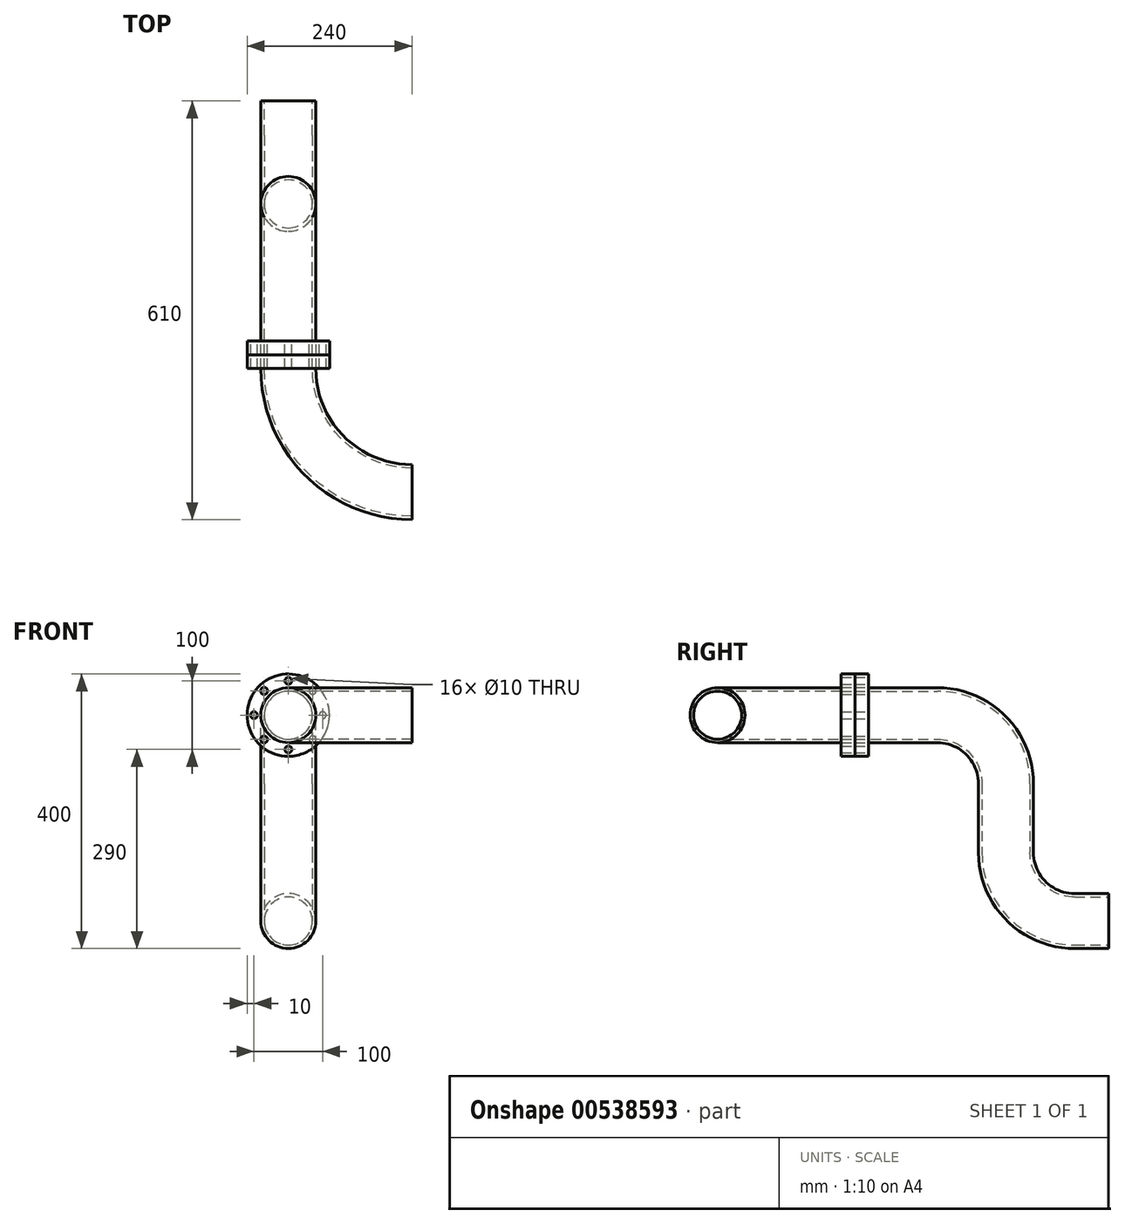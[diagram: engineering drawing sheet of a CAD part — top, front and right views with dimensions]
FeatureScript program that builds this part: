
annotation { "Feature Type Name" : "Feature", "Feature Type Description" : "" }
export const myFeature = defineFeature(function(context is Context, id is Id, definition is map)
    precondition{}
    {
        {
            var Q0;
            Q0=qCreatedBy(makeId("Front.planeOp"),FACE);
            var sketch = newSketch(context, id + "F0", { "sketchPlane" : qUnion([Q0])});
            skCircle(sketch, "E0", {"center": v(0, 0) * mm, "radius": 60 * mm});
            skCircle(sketch, "E1", {"center": v(0, 50) * mm, "radius": 5 * mm});
            skCircle(sketch, "E2", {"center": v(0, -50) * mm, "radius": 5 * mm});
            skCircle(sketch, "E3", {"center": v(-50, 0) * mm, "radius": 5 * mm});
            skCircle(sketch, "E4.1.0", {"center": v(-35.36, 35.36) * mm, "radius": 5 * mm});
            skCircle(sketch, "E5.1.3.0", {"center": v(-35.36, -35.36) * mm, "radius": 5 * mm});
            skCircle(sketch, "E5.1.5.0", {"center": v(35.36, -35.36) * mm, "radius": 5 * mm});
            skCircle(sketch, "E5.1.7.0", {"center": v(35.36, 35.36) * mm, "radius": 5 * mm});
            skCircle(sketch, "E6", {"center": v(50, 0) * mm, "radius": 5 * mm});
            skCircle(sketch, "E7", {"center": v(0, 0) * mm, "radius": 35 * mm});
            skSolve(sketch);
        }
        {
            var Q0;
            Q0=makeQuery(id+"F0.imprint","IMPRINT",FACE,{"disambiguationData":[TD([[makeQuery(id+"F0.imprint","IMPRINT",EDGE,{"derivedFrom":sQuery(id+"F0.wireOp",EDGE,"E0")}),1.0]])]});
            extrude(context, id + "F1", {"entities" : qUnion([Q0]), "depth" : 20 * mm, "offsetDistance" : 25 * mm});
        }
        {
            var Q0;
            Q0=qCreatedBy(makeId("Front.planeOp"),FACE);
            var sketch = newSketch(context, id + "F2", { "sketchPlane" : qUnion([Q0])});
            skCircle(sketch, "E8", {"center": v(0, 0) * mm, "radius": 35 * mm});
            skCircle(sketch, "E9", {"center": v(0, 0) * mm, "radius": 40 * mm});
            skSolve(sketch);
        }
        {
            var Q0;
            Q0=qCreatedBy(makeId("Right.planeOp"),FACE);
            var sketch = newSketch(context, id + "F3", { "sketchPlane" : qUnion([Q0])});
            skLineSegment(sketch, "E10", {"start": v(0, 0) * mm, "end": v(100, 0) * mm});
            skLineSegment(sketch, "E11", {"start": v(200, -100) * mm, "end": v(200, -200) * mm});
            skLineSegment(sketch, "E12", {"start": v(300, -300) * mm, "end": v(350, -300) * mm});
            skPoint(sketch, "E13.visualSharp", {"position": v(200, 0) * mm});
            skArc(sketch, "E13.filletArc", {"start": v(200, -100) * mm, "mid": v(170.71, -29.29) * mm, "end": v(100, 0) * mm});
            skPoint(sketch, "E14.visualSharp", {"position": v(200, -300) * mm});
            skArc(sketch, "E14.filletArc", {"start": v(200, -200) * mm, "mid": v(229.29, -270.71) * mm, "end": v(300, -300) * mm});
            skSolve(sketch);
        }
        {
            var Q0;
            Q0=makeQuery(id+"F2.imprint","IMPRINT",FACE,{"disambiguationData":[TD([[makeQuery(id+"F2.imprint","IMPRINT",EDGE,{"derivedFrom":sQuery(id+"F2.wireOp",EDGE,"E8")}),-1.0]])]});
            var Q1;
            Q1=sQuery(id+"F3.wireOp",EDGE,"E10");
            var Q2;
            Q2=sQuery(id+"F3.wireOp",EDGE,"E13.filletArc");
            var Q3;
            Q3=sQuery(id+"F3.wireOp",EDGE,"E11");
            var Q4;
            Q4=sQuery(id+"F3.wireOp",EDGE,"E14.filletArc");
            var Q5;
            Q5=sQuery(id+"F3.wireOp",EDGE,"E12");
            sweep(context, id + "F4", {"operationType" : NewBodyOperationType.ADD, "profiles" : qUnion([Q0]), "path" : qUnion([Q1, Q2, Q3, Q4, Q5])});
        }
        {
            var Q0;
            Q0=makeQuery(id+"F1.opExtrude","CAP_FACE",FACE,{"disambiguationData":[OSD([sQuery(id+"F0.wireOp",EDGE,"E0"),sQuery(id+"F0.wireOp",EDGE,"E1"),sQuery(id+"F0.wireOp",EDGE,"E2"),sQuery(id+"F0.wireOp",EDGE,"E3"),sQuery(id+"F0.wireOp",EDGE,"E4.1.0"),sQuery(id+"F0.wireOp",EDGE,"E5.1.3.0"),sQuery(id+"F0.wireOp",EDGE,"E5.1.5.0"),sQuery(id+"F0.wireOp",EDGE,"E5.1.7.0"),sQuery(id+"F0.wireOp",EDGE,"E6"),sQuery(id+"F0.wireOp",EDGE,"E7")])],"isStart":false});
            extrude(context, id + "F5", {"entities" : qUnion([Q0]), "depth" : 20 * mm, "offsetDistance" : 25 * mm});
        }
        {
            var Q0;
            Q0=makeQuery(id+"F5.opExtrude","CAP_FACE",FACE,{"disambiguationData":[OSD([sQuery(id+"F0.wireOp",EDGE,"E0"),sQuery(id+"F0.wireOp",EDGE,"E1"),sQuery(id+"F0.wireOp",EDGE,"E2"),sQuery(id+"F0.wireOp",EDGE,"E3"),sQuery(id+"F0.wireOp",EDGE,"E4.1.0"),sQuery(id+"F0.wireOp",EDGE,"E5.1.3.0"),sQuery(id+"F0.wireOp",EDGE,"E5.1.5.0"),sQuery(id+"F0.wireOp",EDGE,"E5.1.7.0"),sQuery(id+"F0.wireOp",EDGE,"E6"),sQuery(id+"F0.wireOp",EDGE,"E7")])],"isStart":false});
            var sketch = newSketch(context, id + "F6", { "sketchPlane" : qUnion([Q0])});
            skCircle(sketch, "E15", {"center": v(0, 0) * mm, "radius": 40 * mm});
            skLineSegment(sketch, "E16", {"start": v(0, 0) * mm, "end": v(180, 0) * mm, "construction": true});
            skLineSegment(sketch, "E17", {"start": v(180, 82.88) * mm, "end": v(180, -123.97) * mm, "construction": true});
            skSolve(sketch);
        }
        {
            var Q0;
            Q0=makeQuery(id+"F6.imprint","IMPRINT",FACE,{"disambiguationData":[TD([[makeQuery(id+"F6.imprint","IMPRINT",EDGE,{"derivedFrom":sQuery(id+"F6.wireOp",EDGE,"E15")}),1.0]])]});
            var Q1;
            Q1=sQuery(id+"F6.wireOp",EDGE,"E17");
            revolve(context, id + "F7", {"operationType" : NewBodyOperationType.ADD, "entities" : qUnion([Q0]), "axis" : qUnion([Q1]), "revolveType" : RevolveType.ONE_DIRECTION, "oppositeDirection" : true, "angle" : 90 * degree});
        }
    });
